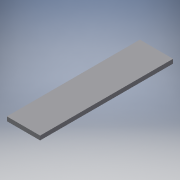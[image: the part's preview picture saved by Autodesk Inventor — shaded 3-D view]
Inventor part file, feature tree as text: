
AUTODESK INVENTOR PART (.ipt)
format: ipt  version: 2017 (Build 210142000, 142)  size: 89,600 bytes
history: native  units: in
note: dims shown in document units (in); Inventor stores cm internally (conversion verified against a paired STEP export)
features: extrude x1, sketch x1
ambient origin geometry x8: Origin, YZ Plane, XZ Plane, XY Plane, X Axis, Y Axis, Z Axis, Center Point
bodies: Solid1 (feature_tree)
feature tree (2):
  extrude  "Extrusion1"  Depth=1.0in
  sketch  "Sketch1"  dims[d0=4.0in d1=1.0in d4=0.125in d5=0.0in]
